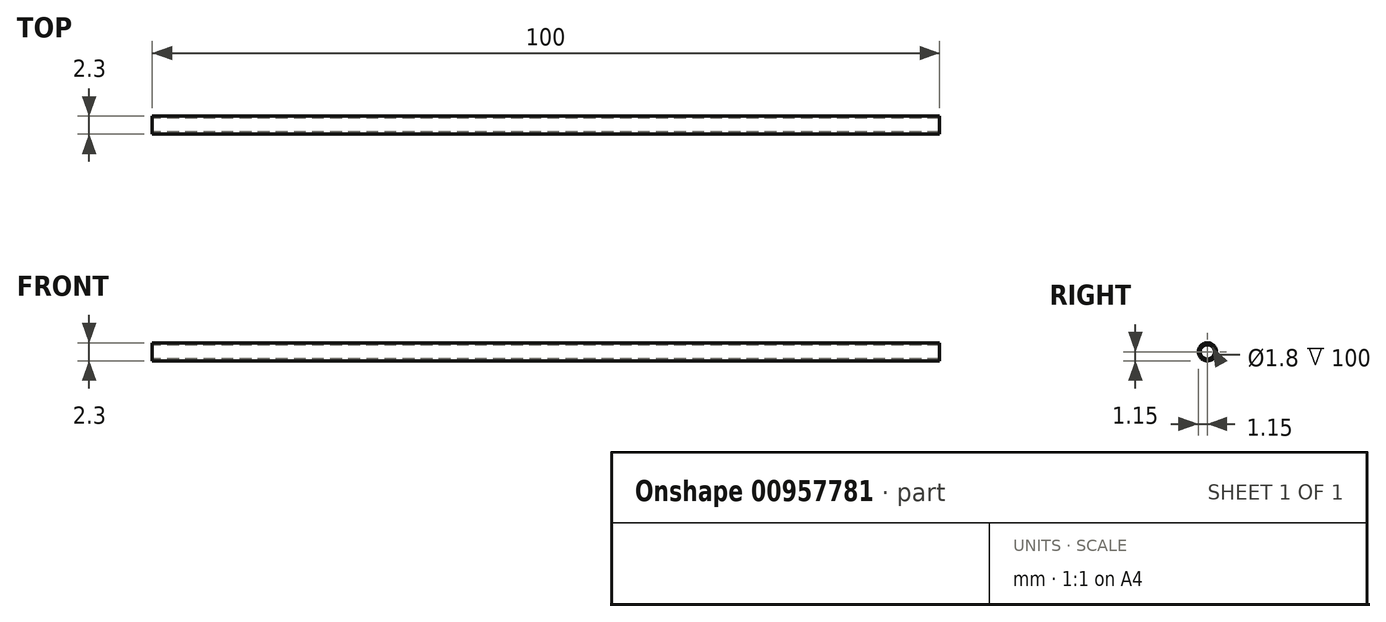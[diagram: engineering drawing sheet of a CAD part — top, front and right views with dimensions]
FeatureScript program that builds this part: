
annotation { "Feature Type Name" : "Feature", "Feature Type Description" : "" }
export const myFeature = defineFeature(function(context is Context, id is Id, definition is map)
    precondition{}
    {
        {
            var Q0;
            Q0=qCreatedBy(makeId("Front.planeOp"),FACE);
            var sketch = newSketch(context, id + "F0", { "sketchPlane" : qUnion([Q0])});
            skLineSegment(sketch, "E0", {"start": v(-6.06, 0) * mm, "end": v(6.25, 0) * mm, "construction": true});
            skLineSegment(sketch, "E1", {"start": v(-5, 0.9) * mm, "end": v(95, 0.9) * mm});
            skLineSegment(sketch, "E2", {"start": v(95, 0.9) * mm, "end": v(95, 1.15) * mm});
            skLineSegment(sketch, "E3", {"start": v(95, 1.15) * mm, "end": v(-5, 1.15) * mm});
            skLineSegment(sketch, "E4", {"start": v(-5, 1.15) * mm, "end": v(-5, 0.9) * mm});
            skSolve(sketch);
        }
        {
            var Q0;
            Q0 = qSketchRegion(id + "F0", true);
            var Q1;
            Q1=sQuery(id+"F0.wireOp",EDGE,"E0");
            revolve(context, id + "F1", {"surfaceOperationType" : NewSurfaceOperationType.NEW, "entities" : qUnion([Q0]), "axis" : qUnion([Q1]), "revolveType" : RevolveType.FULL});
        }
    });
